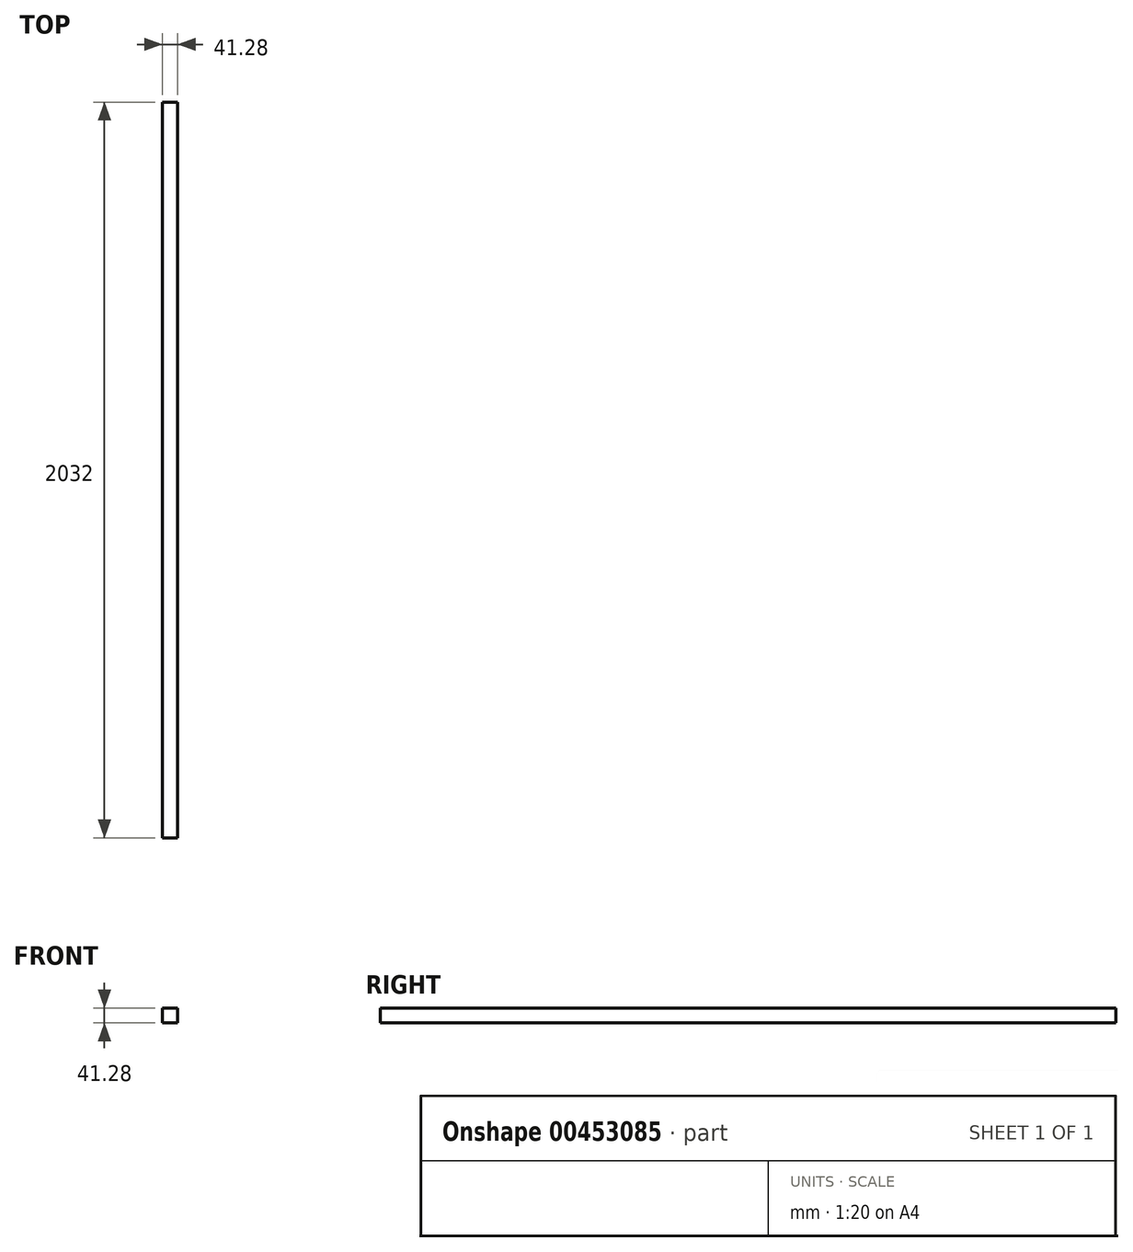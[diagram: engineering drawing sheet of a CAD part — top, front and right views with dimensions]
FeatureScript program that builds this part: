
annotation { "Feature Type Name" : "Feature", "Feature Type Description" : "" }
export const myFeature = defineFeature(function(context is Context, id is Id, definition is map)
    precondition{}
    {
        {
            var Q0;
            Q0=qCreatedBy(makeId("Front.planeOp"),FACE);
            var sketch = newSketch(context, id + "F0", { "sketchPlane" : qUnion([Q0])});
            skLineSegment(sketch, "E0.bottom", {"start": v(20.64, 20.64) * mm, "end": v(-20.64, 20.64) * mm});
            skLineSegment(sketch, "E0.top", {"start": v(20.64, -20.64) * mm, "end": v(-20.64, -20.64) * mm});
            skLineSegment(sketch, "E0.left", {"start": v(20.64, 20.64) * mm, "end": v(20.64, -20.64) * mm});
            skLineSegment(sketch, "E0.right", {"start": v(-20.64, 20.64) * mm, "end": v(-20.64, -20.64) * mm});
            skPoint(sketch, "E0.middle", {"position": v(0, 0) * mm});
            skSolve(sketch);
        }
        {
            var Q0;
            Q0 = qSketchRegion(id + "F0", true);
            extrude(context, id + "F1", {"entities" : qUnion([Q0]), "depth" : 2032 * mm, "offsetDistance" : 25.4 * mm});
        }
    });
